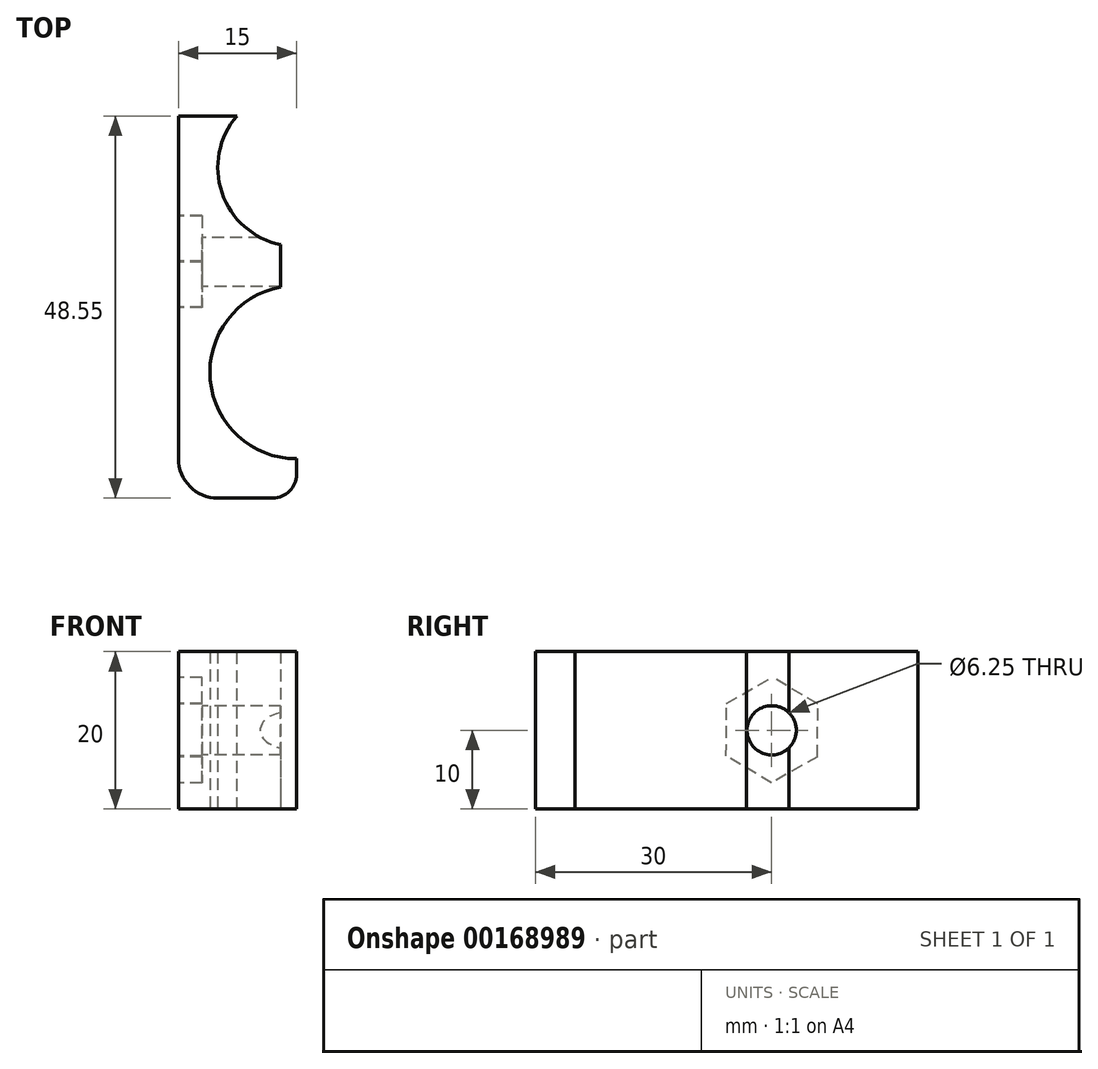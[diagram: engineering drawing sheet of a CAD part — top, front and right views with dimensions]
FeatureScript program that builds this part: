
annotation { "Feature Type Name" : "Feature", "Feature Type Description" : "" }
export const myFeature = defineFeature(function(context is Context, id is Id, definition is map)
    precondition{}
    {
        {
            var Q0;
            Q0=qCreatedBy(makeId("Top.planeOp"),FACE);
            var sketch = newSketch(context, id + "F0", { "sketchPlane" : qUnion([Q0])});
            skCircle(sketch, "E0", {"center": v(0, -36) * mm, "radius": 11 * mm});
            skLineSegment(sketch, "E1", {"start": v(0, -47) * mm, "end": v(0, -25) * mm});
            skLineSegment(sketch, "E2", {"start": v(0, -47) * mm, "end": v(0, -52) * mm});
            skLineSegment(sketch, "E3", {"start": v(0, -52) * mm, "end": v(-15, -52) * mm});
            skLineSegment(sketch, "E4", {"start": v(-15, -52) * mm, "end": v(-15, 6) * mm});
            skLineSegment(sketch, "E5", {"start": v(-15, 6) * mm, "end": v(0, 6) * mm});
            skLineSegment(sketch, "E6", {"start": v(0, 6) * mm, "end": v(0, 0) * mm});
            skCircle(sketch, "E7", {"center": v(0, -10) * mm, "radius": 10 * mm});
            skLineSegment(sketch, "E8", {"start": v(0, -25) * mm, "end": v(0, -20) * mm});
            skLineSegment(sketch, "E9", {"start": v(0, -20) * mm, "end": v(0, 0) * mm});
            skLineSegment(sketch, "E10", {"start": v(0, -22.5) * mm, "end": v(-15, -22.5) * mm});
            skSolve(sketch);
        }
        {
            var Q0;
            {var subQ5=sQuery(id+"F0.wireOp",EDGE,"E5");Q0=makeQuery(id+"F0.imprint","IMPRINT",FACE,{"disambiguationData":[TD([[makeQuery(id+"F0.imprint","IMPRINT",EDGE,{"derivedFrom":subQ5}),-1.0]])]});}
            extrude(context, id + "F1", {"entities" : qUnion([Q0]), "depth" : 20 * mm});
        }
        {
            var Q0;
            {var subQ3=sQuery(id+"F0.wireOp",EDGE,"E2");Q0=makeQuery(id+"F0.imprint","IMPRINT",FACE,{"disambiguationData":[TD([[makeQuery(id+"F0.imprint","IMPRINT",EDGE,{"derivedFrom":subQ3}),-1.0]])]});}
            extrude(context, id + "F2", {"entities" : qUnion([Q0]), "operationType" : NewBodyOperationType.ADD, "depth" : 20 * mm});
        }
        {
            var Q0;
            Q0=makeQuery(id+"F1.opExtrude","SWEPT_FACE",FACE,{"disambiguationData":[OSD([sQuery(id+"F0.wireOp",EDGE,"E6")])]});
            extrude(context, id + "F3", {"entities" : qUnion([Q0]), "operationType" : NewBodyOperationType.REMOVE, "oppositeDirection" : true, "depth" : 1 * mm});
        }
        {
            var Q0;
            Q0=makeQuery(id+"F3.boolean.opBoolean","COPY",FACE,{"derivedFrom":makeQuery(id+"F3.opExtrude","SWEPT_FACE",FACE,{"disambiguationData":[OSD([sQuery(id+"F0.wireOp",EDGE,"E6"),sQuery(id+"F0.wireOp",EDGE,"E7"),sQuery(id+"F0.wireOp",EDGE,"E9")])]})});
            extrude(context, id + "F4", {"entities" : qUnion([Q0]), "operationType" : NewBodyOperationType.REMOVE, "oppositeDirection" : true, "depth" : 2 * mm});
        }
        {
            var Q0;
            Q0=makeQuery(id+"F2.opExtrude","SWEPT_EDGE",EDGE,{"disambiguationData":[OSD([sQuery(id+"F0.wireOp",EDGE,"E3"),sQuery(id+"F0.wireOp",EDGE,"E4")])]});
            fillet(context, id + "F5", {"entities" : qUnion([Q0]), "radius" : 5 * mm, "tangentPropagation" : true, "allowEdgeOverflow" : false});
        }
        {
            var Q0;
            {var subQ0=sQuery(id+"F0.wireOp",EDGE,"E4");Q0=makeQuery(id+"F2.boolean.opBoolean","MERGE",FACE,{"derivedFrom":[makeQuery(id+"F1.opExtrude","SWEPT_FACE",FACE,{"disambiguationData":[OSD([subQ0])]}),makeQuery(id+"F2.opExtrude","SWEPT_FACE",FACE,{"disambiguationData":[OSD([subQ0])]})]});}
            var sketch = newSketch(context, id + "F6", { "sketchPlane" : qUnion([Q0])});
            skCircle(sketch, "E11", {"center": v(22, 10) * mm, "radius": 3.12 * mm});
            skPoint(sketch, "E11.centerSnap0", {"position": v(22, 45.51) * mm});
            skLineSegment(sketch, "E12", {"start": v(16.18, 6.65) * mm, "end": v(16.13, 13.35) * mm});
            skLineSegment(sketch, "E13", {"start": v(16.13, 13.35) * mm, "end": v(21.91, 16.74) * mm});
            skLineSegment(sketch, "E14", {"start": v(16.18, 6.65) * mm, "end": v(22, 3.34) * mm});
            skLineSegment(sketch, "E15", {"start": v(22, 3.34) * mm, "end": v(27.78, 6.73) * mm});
            skLineSegment(sketch, "E16", {"start": v(27.78, 6.73) * mm, "end": v(27.74, 13.43) * mm});
            skLineSegment(sketch, "E17", {"start": v(27.74, 13.43) * mm, "end": v(21.91, 16.74) * mm});
            skPoint(sketch, "E18", {"position": v(16.15, 10) * mm});
            skLineSegment(sketch, "E19", {"start": v(-6, 0) * mm, "end": v(22, 0) * mm});
            skSolve(sketch);
        }
        {
            var Q0;
            {var subQ7=sQuery(id+"F6.wireOp",EDGE,"E15");Q0=makeQuery(id+"F6.imprint","IMPRINT",FACE,{"disambiguationData":[TD([[makeQuery(id+"F6.imprint","IMPRINT",EDGE,{"derivedFrom":subQ7}),1.0]])]});}
            var Q1;
            Q1=makeQuery(id+"F6.imprint","IMPRINT",FACE,{"disambiguationData":[TD([[makeQuery(id+"F6.imprint","IMPRINT",EDGE,{"derivedFrom":sQuery(id+"F6.wireOp",EDGE,"E12")}),-1.0]])]});
            extrude(context, id + "F7", {"entities" : qUnion([Q0, Q1]), "operationType" : NewBodyOperationType.REMOVE, "oppositeDirection" : true, "depth" : 3 * mm});
        }
        {
            var Q0;
            {var subQ0=sQuery(id+"F0.wireOp",EDGE,"E10");var subQ1=sQuery(id+"F0.wireOp",EDGE,"E8");var subQ2=sQuery(id+"F0.wireOp",EDGE,"E4");Q0=makeQuery(id+"F2.boolean.opBoolean","MERGE",FACE,{"derivedFrom":[makeQuery(id+"F1.opExtrude","CAP_FACE",FACE,{"disambiguationData":[OSD([subQ2,sQuery(id+"F0.wireOp",EDGE,"E5"),sQuery(id+"F0.wireOp",EDGE,"E6"),sQuery(id+"F0.wireOp",EDGE,"E7"),subQ1,subQ0])],"isStart":false}),makeQuery(id+"F2.opExtrude","CAP_FACE",FACE,{"disambiguationData":[OSD([sQuery(id+"F0.wireOp",EDGE,"E0"),sQuery(id+"F0.wireOp",EDGE,"E2"),sQuery(id+"F0.wireOp",EDGE,"E3"),subQ2,subQ1,subQ0])],"isStart":false})]});}
            var sketch = newSketch(context, id + "F8", { "sketchPlane" : qUnion([Q0])});
            skLineSegment(sketch, "E20", {"start": v(-15, -3.45) * mm, "end": v(-7.56, -3.45) * mm});
            skSolve(sketch);
        }
        {
            var Q0;
            {var subQ5=sQuery(id+"F8.wireOp",EDGE,"E20");Q0=makeQuery(id+"F8.imprint","IMPRINT",FACE,{"disambiguationData":[TD([[makeQuery(id+"F8.imprint","IMPRINT",EDGE,{"derivedFrom":subQ5}),1.0]])]});}
            extrude(context, id + "F9", {"entities" : qUnion([Q0]), "operationType" : NewBodyOperationType.REMOVE, "endBound" : BoundingType.UP_TO_NEXT, "oppositeDirection" : true, "depth" : 25 * mm});
        }
        {
            var Q0;
            {var subQ0=sQuery(id+"F0.wireOp",EDGE,"E8");Q0=makeQuery(id+"F2.boolean.opBoolean","MERGE",FACE,{"derivedFrom":[makeQuery(id+"F1.opExtrude","SWEPT_FACE",FACE,{"disambiguationData":[OSD([subQ0])]}),makeQuery(id+"F2.opExtrude","SWEPT_FACE",FACE,{"disambiguationData":[OSD([subQ0])]})]});}
            extrude(context, id + "F10", {"entities" : qUnion([Q0]), "operationType" : NewBodyOperationType.REMOVE, "oppositeDirection" : true, "depth" : 2 * mm});
        }
        {
            var Q0;
            Q0=makeQuery(id+"F10.boolean.opBoolean","COPY",FACE,{"derivedFrom":makeQuery(id+"F10.opExtrude","SWEPT_FACE",FACE,{"disambiguationData":[OSD([sQuery(id+"F0.wireOp",EDGE,"E7"),sQuery(id+"F0.wireOp",EDGE,"E8"),sQuery(id+"F0.wireOp",EDGE,"E9")])]})});
            extrude(context, id + "F11", {"entities" : qUnion([Q0]), "operationType" : NewBodyOperationType.REMOVE, "endBound" : BoundingType.UP_TO_NEXT, "oppositeDirection" : true, "depth" : 25 * mm});
        }
        {
            var Q0;
            Q0=makeQuery(id+"F10.boolean.opBoolean","COPY",FACE,{"derivedFrom":makeQuery(id+"F10.opExtrude","SWEPT_FACE",FACE,{"disambiguationData":[OSD([sQuery(id+"F0.wireOp",EDGE,"E0"),sQuery(id+"F0.wireOp",EDGE,"E1"),sQuery(id+"F0.wireOp",EDGE,"E8")])]})});
            extrude(context, id + "F12", {"entities" : qUnion([Q0]), "operationType" : NewBodyOperationType.REMOVE, "endBound" : BoundingType.UP_TO_NEXT, "oppositeDirection" : true, "depth" : 25 * mm});
        }
        {
            var Q0;
            Q0=makeQuery(id+"F2.opExtrude","SWEPT_EDGE",EDGE,{"disambiguationData":[OSD([sQuery(id+"F0.wireOp",EDGE,"E2"),sQuery(id+"F0.wireOp",EDGE,"E3")])]});
            fillet(context, id + "F13", {"entities" : qUnion([Q0]), "radius" : 3 * mm, "tangentPropagation" : true, "allowEdgeOverflow" : false});
        }
        {
            var Q0;
            {var subQ0=sQuery(id+"F0.wireOp",EDGE,"E4");Q0=makeQuery(id+"F7.boolean.opBoolean","SPLIT",FACE,{"disambiguationData":[TD([makeQuery(id+"F7.opExtrude","SWEPT_FACE",FACE,{"disambiguationData":[OSD([sQuery(id+"F6.wireOp",EDGE,"E11")])]})])],"derivedFrom":makeQuery(id+"F2.boolean.opBoolean","MERGE",FACE,{"derivedFrom":[makeQuery(id+"F1.opExtrude","SWEPT_FACE",FACE,{"disambiguationData":[OSD([subQ0])]}),makeQuery(id+"F2.opExtrude","SWEPT_FACE",FACE,{"disambiguationData":[OSD([subQ0])]})]})});}
            extrude(context, id + "F14", {"entities" : qUnion([Q0]), "operationType" : NewBodyOperationType.REMOVE, "endBound" : BoundingType.UP_TO_NEXT, "oppositeDirection" : true, "depth" : 25 * mm});
        }
    });
